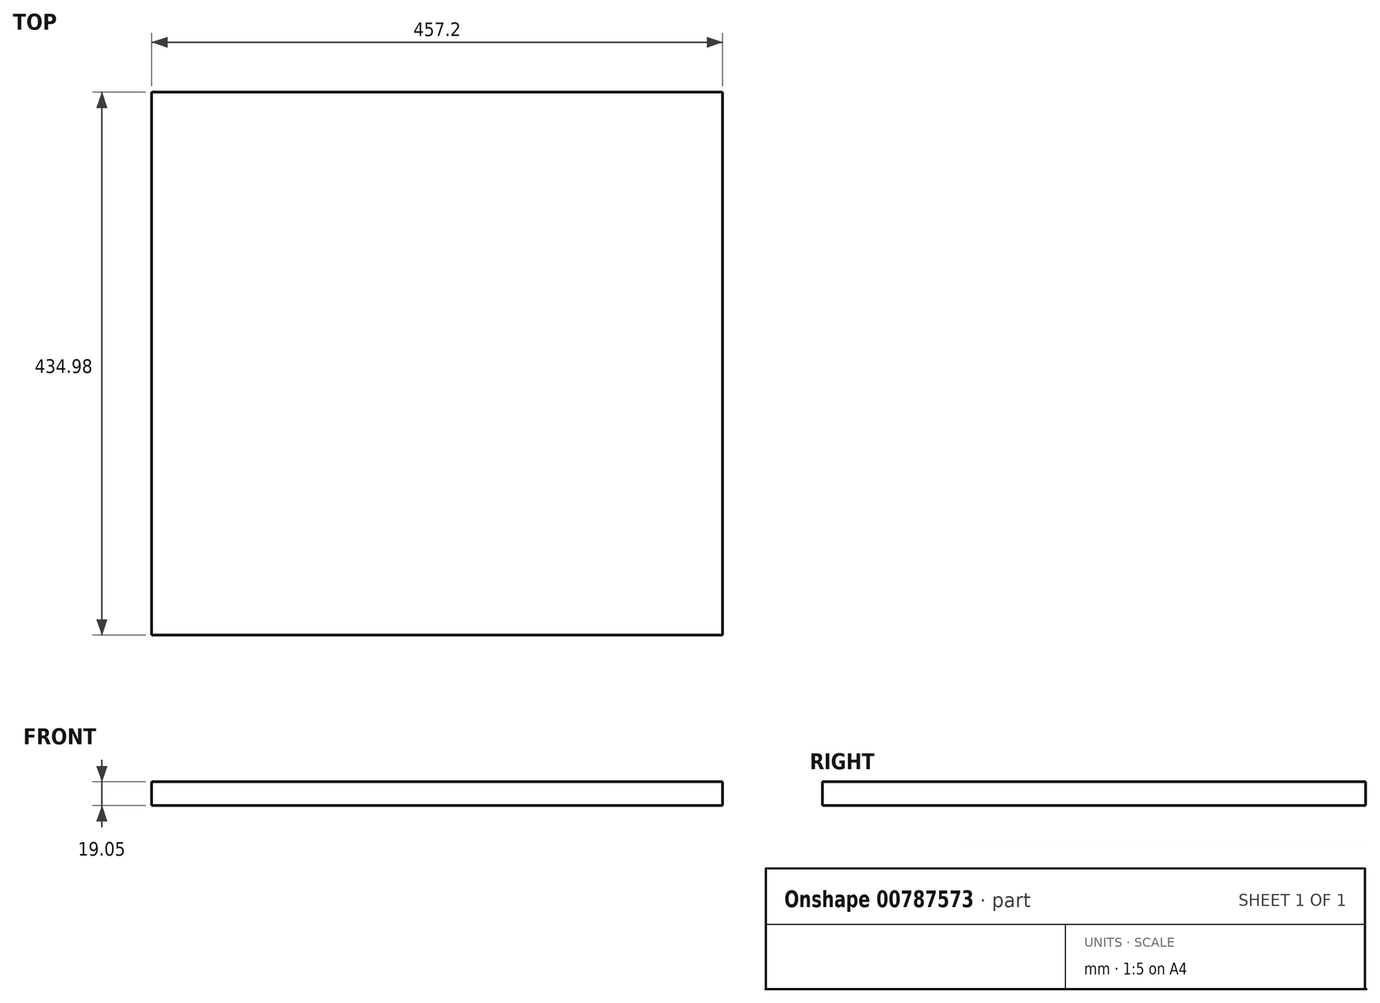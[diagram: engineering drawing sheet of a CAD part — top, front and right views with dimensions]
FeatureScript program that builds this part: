
annotation { "Feature Type Name" : "Feature", "Feature Type Description" : "" }
export const myFeature = defineFeature(function(context is Context, id is Id, definition is map)
    precondition{}
    {
        {
            var Q0;
            Q0=qCreatedBy(makeId("Top.planeOp"),FACE);
            var sketch = newSketch(context, id + "F0", { "sketchPlane" : qUnion([Q0])});
            skLineSegment(sketch, "E0.bottom", {"start": v(228.6, -217.49) * mm, "end": v(-228.6, -217.49) * mm});
            skLineSegment(sketch, "E0.top", {"start": v(228.6, 217.49) * mm, "end": v(-228.6, 217.49) * mm});
            skLineSegment(sketch, "E0.left", {"start": v(228.6, -217.49) * mm, "end": v(228.6, 217.49) * mm});
            skLineSegment(sketch, "E0.right", {"start": v(-228.6, -217.49) * mm, "end": v(-228.6, 217.49) * mm});
            skPoint(sketch, "E0.middle", {"position": v(0, 0) * mm});
            skSolve(sketch);
        }
        {
            var Q0;
            Q0 = qSketchRegion(id + "F0", true);
            extrude(context, id + "F1", {"entities" : qUnion([Q0]), "depth" : 19.05 * mm, "offsetDistance" : 25.4 * mm});
        }
    });
